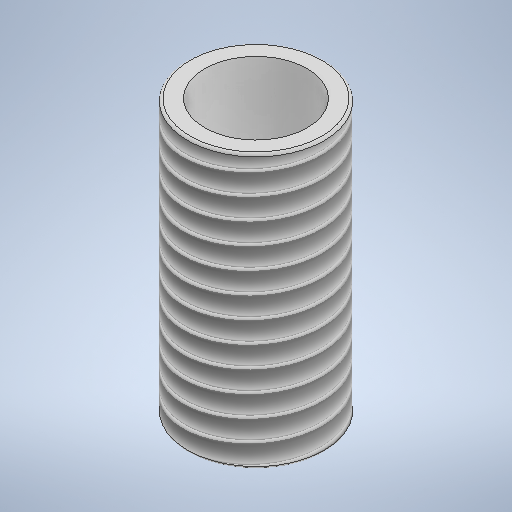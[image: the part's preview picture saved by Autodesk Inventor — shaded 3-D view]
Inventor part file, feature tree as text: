
AUTODESK INVENTOR PART (.ipt)
format: ipt  version: 2025.1 (Build 291241000, 241)  size: 316,416 bytes
history: native  units: mm
features: extrude x1, thread x1, fillet x1, sketch x1
ambient origin geometry x8: Origin, YZ Plane, XZ Plane, XY Plane, X Axis, Y Axis, Z Axis, Center Point
bodies: Solid1 (feature_tree)
feature tree (4):
  extrude  "Extrusion1"  Depth=0.15mm
  thread  "Thread1"  [1 undecoded]
  fillet  "Fillet1"  Radius=16.0mm
  sketch  "Sketch1"  dims[d0=8.0mm d1=6.0mm d2=16.0mm d3=0.0mm d4=16.0mm d5=0.0mm d6=0.15mm]
note: 1 required parameter value undecoded (feature->parameter linkage not recoverable at this tier; creation-order binding heuristic only, values carry confidence <= 0.55)
